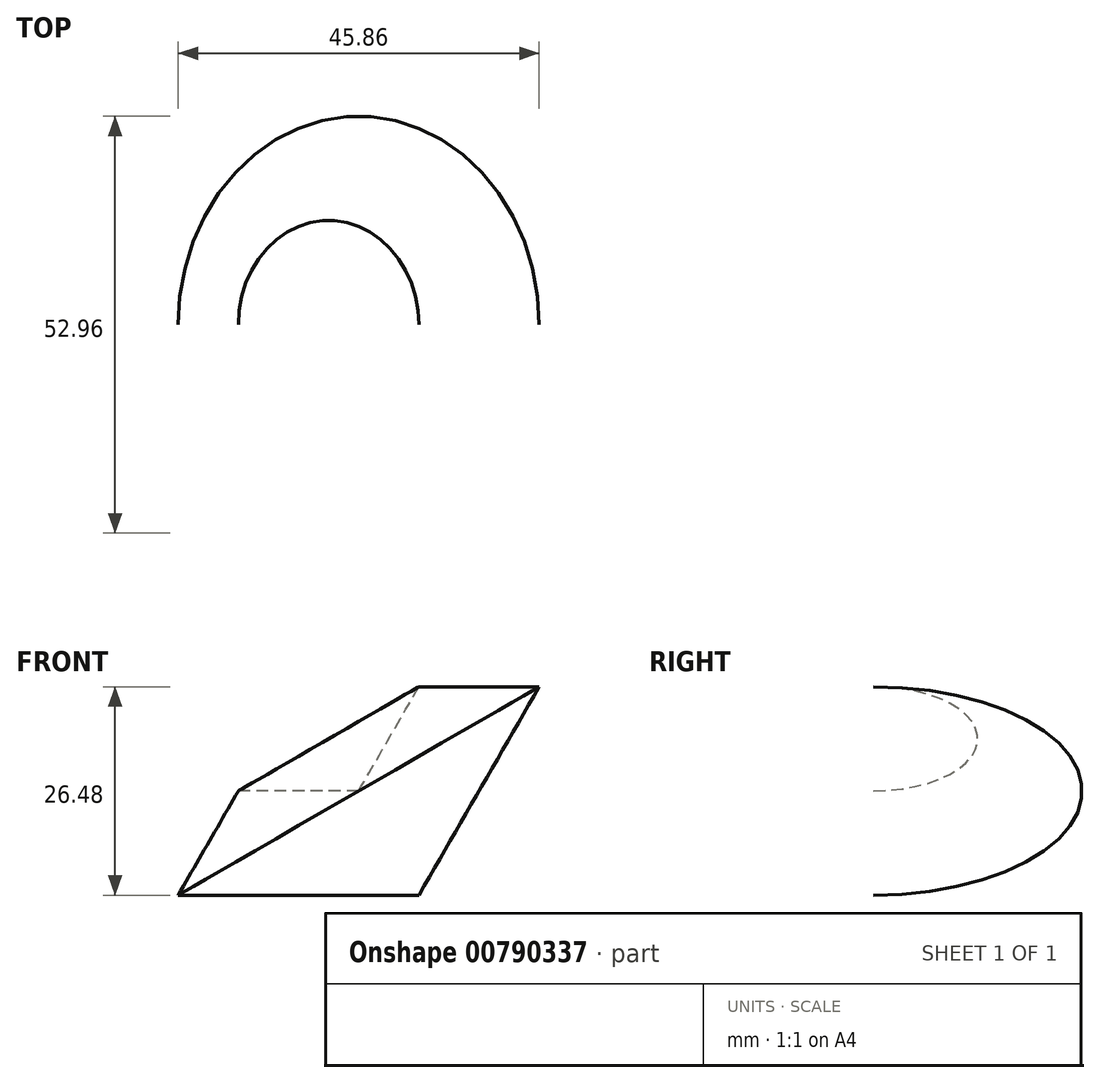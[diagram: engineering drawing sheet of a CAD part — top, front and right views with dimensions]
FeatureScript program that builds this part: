
annotation { "Feature Type Name" : "Feature", "Feature Type Description" : "" }
export const myFeature = defineFeature(function(context is Context, id is Id, definition is map)
    precondition{}
    {
        {
            var Q0;
            Q0=qCreatedBy(makeId("Front.planeOp"),FACE);
            var sketch = newSketch(context, id + "F0", { "sketchPlane" : qUnion([Q0])});
            skCircle(sketch, "E0.cCircle", {"center": v(0, 0) * mm, "radius": 13.24 * mm, "construction": true});
            skLineSegment(sketch, "E0.0", {"start": v(7.64, -13.24) * mm, "end": v(-7.64, -13.24) * mm});
            skLineSegment(sketch, "E0.1", {"start": v(-7.64, -13.24) * mm, "end": v(-15.29, 0) * mm});
            skLineSegment(sketch, "E0.2", {"start": v(-15.29, 0) * mm, "end": v(-7.64, 13.24) * mm});
            skLineSegment(sketch, "E0.3", {"start": v(-7.64, 13.24) * mm, "end": v(7.64, 13.24) * mm});
            skLineSegment(sketch, "E0.4", {"start": v(7.64, 13.24) * mm, "end": v(15.29, 0) * mm});
            skLineSegment(sketch, "E0.5", {"start": v(15.29, 0) * mm, "end": v(7.64, -13.24) * mm});
            skPoint(sketch, "E0.0.midPoint", {"position": v(0, -13.24) * mm});
            skLineSegment(sketch, "E1", {"start": v(7.64, 13.24) * mm, "end": v(-7.64, -13.24) * mm});
            skSolve(sketch);
        }
        {
            var Q0;
            Q0=makeQuery(id+"F0.imprint","IMPRINT",FACE,{"disambiguationData":[TD([[makeQuery(id+"F0.imprint","IMPRINT",EDGE,{"derivedFrom":sQuery(id+"F0.wireOp",EDGE,"E0.1")}),-1.0]])]});
            var Q1;
            Q1=sQuery(id+"F0.wireOp",EDGE,"E0.1");
            revolve(context, id + "F1", {"surfaceOperationType" : NewSurfaceOperationType.NEW, "entities" : qUnion([Q0]), "axis" : qUnion([Q1]), "revolveType" : RevolveType.FULL});
        }
    });
